# Revit family: FU_Table_Sandler_Lan XL 8-1
name_source: partatom
category: Furniture
units: mm (PartAtom-declared; Revit-internal decimal feet)

## family parameters
Always vertical = Yes
Cut with Voids When Loaded = No
OmniClass Number = 23.40.20.00
OmniClass Title = General Furniture and Specialties
Room Calculation Point = No
Shared = No
Work Plane-Based = No

## types (1)
- Lan XL 8.1
    Base Finish = Epoxy - M1_B00 - Black
    Default Elevation = 0 mm  [stored 0 ft]
    Depth = 350 mm  [stored 1.14829 ft]
    Description = Multi purpose table with painted steel base and lacquered top.
    Height = 660 mm
    Manufacturer = Sandler
    Model = Lan XL 8.1
    Top Finish = Wood - Oak - Natural - V
    URL = https://www.sandlerseating.com
    Width = 550 mm  [stored 1.80446 ft]

note: [stored X ft] marks values corroborated as IEEE doubles in the binary element streams (Revit-internal decimal feet)

## geometry (parser evidence)
native form markers: Sweep x3
no freeform markers — native parametric forms only
